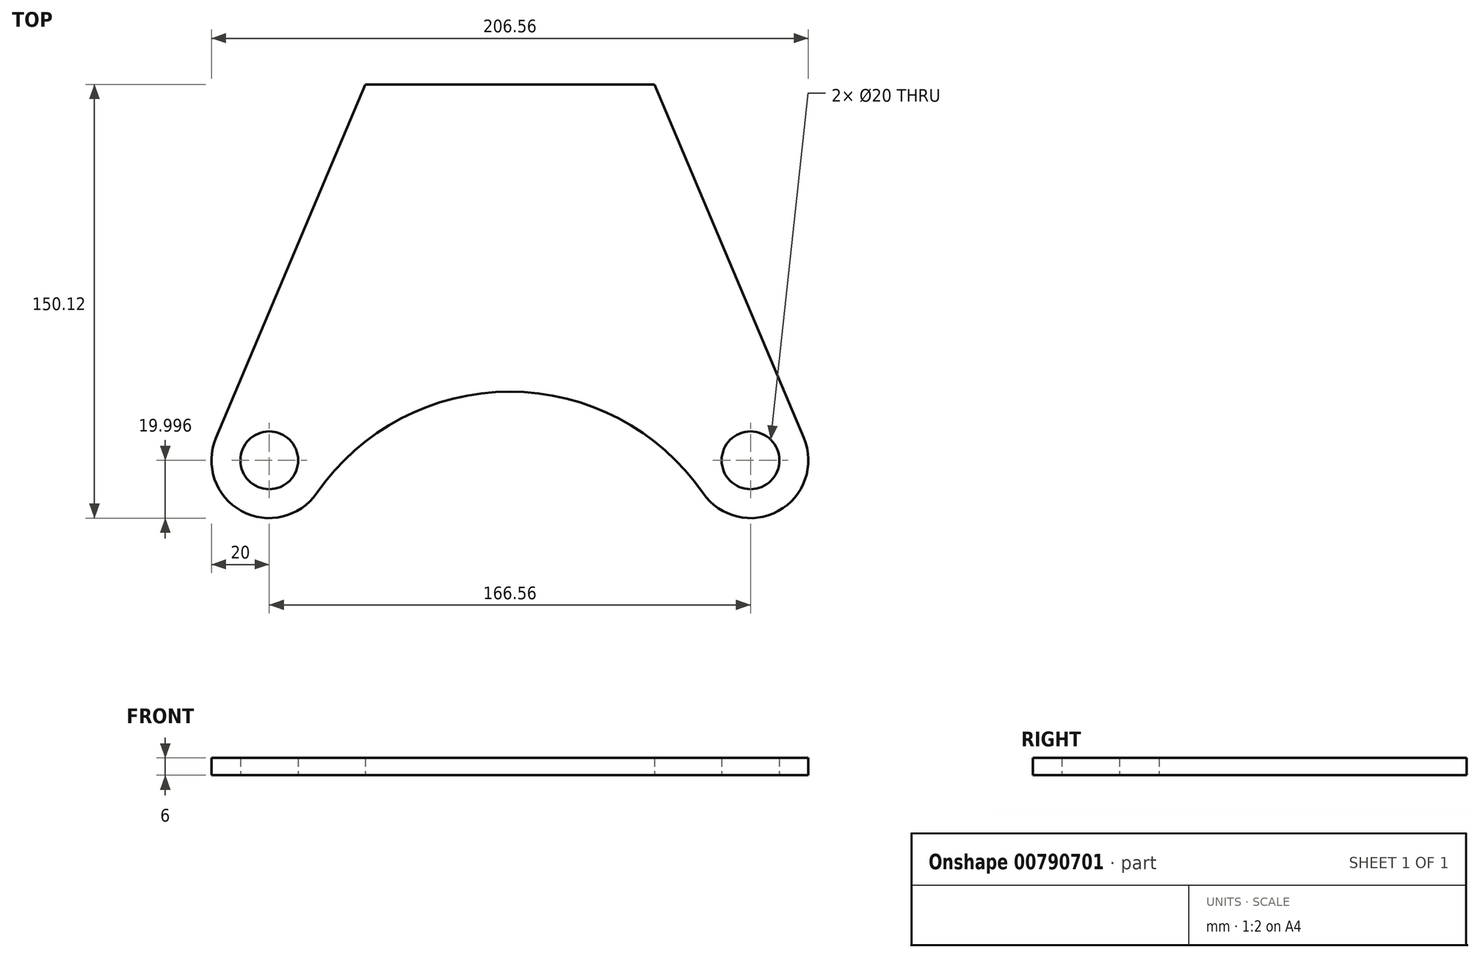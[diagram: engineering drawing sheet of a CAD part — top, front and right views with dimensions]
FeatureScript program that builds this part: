
annotation { "Feature Type Name" : "Feature", "Feature Type Description" : "" }
export const myFeature = defineFeature(function(context is Context, id is Id, definition is map)
    precondition{}
    {
        {
            var Q0;
            Q0=qCreatedBy(makeId("Top.planeOp"),FACE);
            var sketch = newSketch(context, id + "F0", { "sketchPlane" : qUnion([Q0])});
            skCircle(sketch, "E0", {"center": v(0, 0) * mm, "radius": 84 * mm});
            skCircle(sketch, "E1", {"center": v(0, -64) * mm, "radius": 20 * mm});
            skCircle(sketch, "E2.1.0", {"center": v(83.28, 80.25) * mm, "radius": 20 * mm});
            skCircle(sketch, "E2.2.0", {"center": v(-83.28, 80.25) * mm, "radius": 20 * mm});
            skPoint(sketch, "E2.center", {"position": v(0, 32.16) * mm});
            skArc(sketch, "E3", {"start": v(66.81, 68.9) * mm, "mid": v(0, 104) * mm, "end": v(-66.81, 68.9) * mm});
            skLineSegment(sketch, "E4", {"start": v(0, 210.37) * mm, "end": v(50, 210.37) * mm});
            skLineSegment(sketch, "E5", {"start": v(0, 210.37) * mm, "end": v(-50, 210.37) * mm});
            skLineSegment(sketch, "E6", {"start": v(-50, 210.37) * mm, "end": v(-101.7, 88.03) * mm});
            skLineSegment(sketch, "E7", {"start": v(50, 210.37) * mm, "end": v(101.7, 88.03) * mm});
            skCircle(sketch, "E8", {"center": v(83.28, 80.25) * mm, "radius": 10 * mm});
            skCircle(sketch, "E9", {"center": v(-83.28, 80.25) * mm, "radius": 10 * mm});
            skCircle(sketch, "E10", {"center": v(83.28, 80.25) * mm, "radius": 23.5 * mm});
            skCircle(sketch, "E11", {"center": v(-83.28, 80.25) * mm, "radius": 23.5 * mm});
            skLineSegment(sketch, "E12", {"start": v(90.84, 113.75) * mm, "end": v(-90.84, 113.75) * mm});
            skCircle(sketch, "E13", {"center": v(0, 0) * mm, "radius": 92.15 * mm});
            skSolve(sketch);
        }
        {
            var Q0;
            {var subQ0=sQuery(id+"F0.wireOp",EDGE,"E2.1.0");var subQ1=makeQuery(id+"F0.imprint","INTERSECT",VERTEX,{"derivedFrom":[subQ0,sQuery(id+"F0.wireOp",EDGE,"E3")]});Q0=makeQuery(id+"F0.imprint","IMPRINT",FACE,{"disambiguationData":[TD([[makeQuery(id+"F0.imprint","IMPRINT",EDGE,{"disambiguationData":[TD([[subQ1,-1.0]])],"derivedFrom":subQ0}),1.0]])]});}
            var Q1;
            {var subQ0=sQuery(id+"F0.wireOp",EDGE,"E3");Q1=makeQuery(id+"F0.imprint","IMPRINT",FACE,{"disambiguationData":[TD([[makeQuery(id+"F0.imprint","IMPRINT",EDGE,{"derivedFrom":subQ0}),-1.0]])]});}
            var Q2;
            {var subQ0=sQuery(id+"F0.wireOp",EDGE,"E2.2.0");var subQ1=makeQuery(id+"F0.imprint","IMPRINT",VERTEX,{"derivedFrom":subQ0});Q2=makeQuery(id+"F0.imprint","IMPRINT",FACE,{"disambiguationData":[TD([[makeQuery(id+"F0.imprint","IMPRINT",EDGE,{"disambiguationData":[TD([[subQ1,-1.0]])],"derivedFrom":subQ0}),1.0]])]});}
            var Q3;
            {var subQ0=sQuery(id+"F0.wireOp",EDGE,"E2.2.0");var subQ1=makeQuery(id+"F0.imprint","INTERSECT",VERTEX,{"derivedFrom":[subQ0,sQuery(id+"F0.wireOp",EDGE,"E3")]});Q3=makeQuery(id+"F0.imprint","IMPRINT",FACE,{"disambiguationData":[TD([[makeQuery(id+"F0.imprint","IMPRINT",EDGE,{"disambiguationData":[TD([[subQ1,1.0]])],"derivedFrom":subQ0}),1.0]])]});}
            var Q4;
            {var subQ4=sQuery(id+"F0.wireOp",EDGE,"E4");Q4=makeQuery(id+"F0.imprint","IMPRINT",FACE,{"disambiguationData":[TD([[makeQuery(id+"F0.imprint","IMPRINT",EDGE,{"derivedFrom":subQ4}),-1.0]])]});}
            var Q5;
            {var subQ5=sQuery(id+"F0.wireOp",EDGE,"E12");Q5=makeQuery(id+"F0.imprint","IMPRINT",FACE,{"disambiguationData":[TD([[makeQuery(id+"F0.imprint","IMPRINT",EDGE,{"derivedFrom":subQ5}),1.0]])]});}
            extrude(context, id + "F1", {"entities" : qUnion([Q0, Q1, Q2, Q3, Q4, Q5]), "depth" : 6 * mm, "offsetDistance" : 25 * mm});
        }
    });
